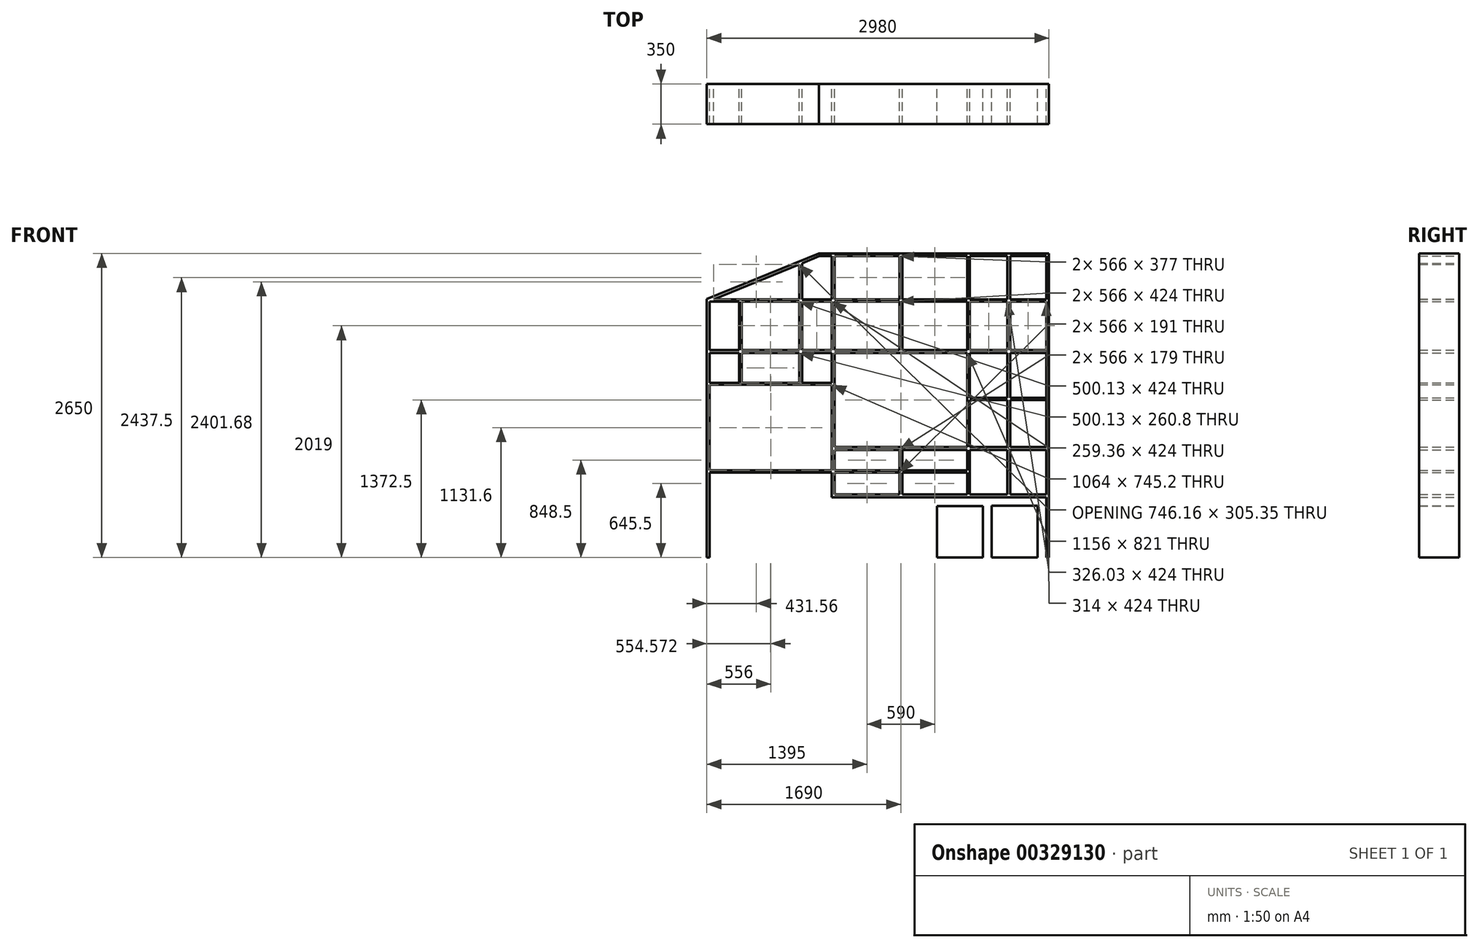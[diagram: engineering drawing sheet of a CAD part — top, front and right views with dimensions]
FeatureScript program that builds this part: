
annotation { "Feature Type Name" : "Feature", "Feature Type Description" : "" }
export const myFeature = defineFeature(function(context is Context, id is Id, definition is map)
    precondition{}
    {
        {
            var Q0;
            Q0=qCreatedBy(makeId("Front.planeOp"),FACE);
            var sketch = newSketch(context, id + "F0", { "sketchPlane" : qUnion([Q0])});
            skLineSegment(sketch, "E0", {"start": v(0, 0) * mm, "end": v(0, 2251) * mm});
            skLineSegment(sketch, "E1", {"start": v(0, 2251) * mm, "end": v(975, 2650) * mm});
            skLineSegment(sketch, "E2", {"start": v(975, 2650) * mm, "end": v(3933.36, 2650) * mm});
            skLineSegment(sketch, "E3", {"start": v(3933.36, 2650) * mm, "end": v(4900, 2240) * mm});
            skLineSegment(sketch, "E4", {"start": v(4900, 2240) * mm, "end": v(4900, 0) * mm});
            skLineSegment(sketch, "E5", {"start": v(4900, 0) * mm, "end": v(0, 0) * mm});
            skLineSegment(sketch, "E6", {"start": v(4550, 0) * mm, "end": v(4550, 2100) * mm});
            skLineSegment(sketch, "E7", {"start": v(4550, 2100) * mm, "end": v(3350, 2100) * mm});
            skLineSegment(sketch, "E8", {"start": v(3350, 2100) * mm, "end": v(3350, 0) * mm});
            skLineSegment(sketch, "E9.bottom", {"start": v(1200, 1695) * mm, "end": v(2180, 1695) * mm});
            skLineSegment(sketch, "E9.top", {"start": v(1200, 1050) * mm, "end": v(2180, 1050) * mm});
            skLineSegment(sketch, "E9.left", {"start": v(1200, 1695) * mm, "end": v(1200, 1050) * mm});
            skLineSegment(sketch, "E9.right", {"start": v(2180, 1695) * mm, "end": v(2180, 1050) * mm});
            skLineSegment(sketch, "E10", {"start": v(2980, 2650) * mm, "end": v(2980, 0) * mm});
            skLineSegment(sketch, "E11", {"start": v(2963, 550) * mm, "end": v(2642, 550) * mm});
            skLineSegment(sketch, "E12.0", {"start": v(24, 0) * mm, "end": v(24, 502) * mm});
            skLineSegment(sketch, "E13.0", {"start": v(979.72, 2626) * mm, "end": v(1088, 2626) * mm});
            skLineSegment(sketch, "E14.0", {"start": v(2963, 526) * mm, "end": v(1088, 526) * mm});
            skLineSegment(sketch, "E15.0", {"start": v(2642, 2636) * mm, "end": v(2642, 2626) * mm});
            skLineSegment(sketch, "E16.0", {"start": v(2291.97, 1807) * mm, "end": v(2291.97, 2231) * mm});
            skLineSegment(sketch, "E17.0", {"start": v(2268, 1807) * mm, "end": v(2268, 2231) * mm});
            skLineSegment(sketch, "E18.0", {"start": v(2268, 1783) * mm, "end": v(2268, 962) * mm});
            skLineSegment(sketch, "E19.0", {"start": v(2292, 1783) * mm, "end": v(2292, 1390.5) * mm});
            skLineSegment(sketch, "E20.0", {"start": v(2292, 938) * mm, "end": v(2292, 540) * mm});
            skLineSegment(sketch, "E21.0", {"start": v(2268, 938) * mm, "end": v(2268, 759) * mm});
            skLineSegment(sketch, "E22.0", {"start": v(1702, 1800) * mm, "end": v(1702, 2231) * mm});
            skLineSegment(sketch, "E23.0", {"start": v(1678, 1800) * mm, "end": v(1678, 2231) * mm});
            skLineSegment(sketch, "E24.0", {"start": v(1112, 1807) * mm, "end": v(1112, 2231) * mm});
            skLineSegment(sketch, "E25.0", {"start": v(1088, 1807) * mm, "end": v(1088, 2231) * mm});
            skLineSegment(sketch, "E26.0", {"start": v(1088, 1783) * mm, "end": v(1088, 1522.2) * mm});
            skLineSegment(sketch, "E27.0", {"start": v(1112, 1783) * mm, "end": v(1112, 1222.6) * mm});
            skLineSegment(sketch, "E28.0", {"start": v(1088, 938) * mm, "end": v(1088, 759) * mm});
            skLineSegment(sketch, "E29.0", {"start": v(1112, 938) * mm, "end": v(1112, 759) * mm});
            skLineSegment(sketch, "E30.0", {"start": v(1105, 1783) * mm, "end": v(2275, 1783) * mm});
            skLineSegment(sketch, "E31.0", {"start": v(1105, 1807) * mm, "end": v(1678, 1807) * mm});
            skLineSegment(sketch, "E32.0", {"start": v(1105, 938) * mm, "end": v(1678, 938) * mm});
            skLineSegment(sketch, "E33.0", {"start": v(1105, 962) * mm, "end": v(2275, 962) * mm});
            skLineSegment(sketch, "E34.0", {"start": v(1095, 1807) * mm, "end": v(822.04, 1807) * mm});
            skLineSegment(sketch, "E35.0", {"start": v(1095, 1783) * mm, "end": v(822.04, 1783) * mm});
            skLineSegment(sketch, "E36.0", {"start": v(2284.97, 938) * mm, "end": v(2625, 938) * mm});
            skLineSegment(sketch, "E37.0", {"start": v(2284.97, 962) * mm, "end": v(2625, 962) * mm});
            skLineSegment(sketch, "E38.0", {"start": v(2284.97, 1783) * mm, "end": v(2625, 1783) * mm});
            skLineSegment(sketch, "E39.0", {"start": v(2284.97, 1807) * mm, "end": v(2625, 1807) * mm});
            skLineSegment(sketch, "E40.0", {"start": v(1678, 945) * mm, "end": v(1678, 759) * mm});
            skLineSegment(sketch, "E41.0", {"start": v(1702, 945) * mm, "end": v(1702, 759) * mm});
            skLineSegment(sketch, "E42.0", {"start": v(17, 2231) * mm, "end": v(280.5, 2231) * mm});
            skLineSegment(sketch, "E43.0", {"start": v(17, 2249) * mm, "end": v(298.67, 2249) * mm});
            skLineSegment(sketch, "E44.0", {"start": v(1095, 1522.2) * mm, "end": v(828.64, 1522.2) * mm});
            skLineSegment(sketch, "E45.0", {"start": v(1095, 1504.2) * mm, "end": v(1088, 1504.2) * mm});
            skLineSegment(sketch, "E46.0", {"start": v(2275, 759) * mm, "end": v(1695, 759) * mm});
            skLineSegment(sketch, "E47.0", {"start": v(2275, 741) * mm, "end": v(1695, 741) * mm});
            skLineSegment(sketch, "E48", {"start": v(1112, 1222.6) * mm, "end": v(1112, 962) * mm});
            skLineSegment(sketch, "E49.bottom", {"start": v(100, 0) * mm, "end": v(500, 0) * mm});
            skLineSegment(sketch, "E49.left", {"start": v(100, 0) * mm, "end": v(100, 450) * mm});
            skLineSegment(sketch, "E49.right", {"start": v(500, 0) * mm, "end": v(500, 450) * mm});
            skLineSegment(sketch, "E50.bottom", {"start": v(576, 0) * mm, "end": v(976, 0) * mm});
            skLineSegment(sketch, "E50.left", {"start": v(576, 0) * mm, "end": v(576, 450) * mm});
            skLineSegment(sketch, "E50.right", {"start": v(976, 0) * mm, "end": v(976, 450) * mm});
            skLineSegment(sketch, "E51.bottom", {"start": v(1052, 0) * mm, "end": v(1452, 0) * mm});
            skLineSegment(sketch, "E51.top", {"start": v(1052, 450) * mm, "end": v(1452, 450) * mm});
            skLineSegment(sketch, "E51.left", {"start": v(1052, 0) * mm, "end": v(1052, 450) * mm});
            skLineSegment(sketch, "E51.right", {"start": v(1452, 0) * mm, "end": v(1452, 450) * mm});
            skLineSegment(sketch, "E52.bottom", {"start": v(1528, 0) * mm, "end": v(1928, 0) * mm});
            skLineSegment(sketch, "E52.top", {"start": v(1528, 450) * mm, "end": v(1928, 450) * mm});
            skLineSegment(sketch, "E52.left", {"start": v(1528, 0) * mm, "end": v(1528, 450) * mm});
            skLineSegment(sketch, "E52.right", {"start": v(1928, 0) * mm, "end": v(1928, 450) * mm});
            skLineSegment(sketch, "E53.bottom", {"start": v(2004, -2.2) * mm, "end": v(2404, -2.2) * mm});
            skLineSegment(sketch, "E53.top", {"start": v(2004, 447.8) * mm, "end": v(2404, 447.8) * mm});
            skLineSegment(sketch, "E53.left", {"start": v(2004, -2.2) * mm, "end": v(2004, 447.8) * mm});
            skLineSegment(sketch, "E53.right", {"start": v(2404, -2.2) * mm, "end": v(2404, 447.8) * mm});
            skLineSegment(sketch, "E54.bottom", {"start": v(2450, 0) * mm, "end": v(2850, 0) * mm});
            skLineSegment(sketch, "E55.bottom", {"start": v(2480, 0) * mm, "end": v(2880, 0) * mm});
            skLineSegment(sketch, "E55.top", {"start": v(2480, 450) * mm, "end": v(2880, 450) * mm});
            skLineSegment(sketch, "E55.left", {"start": v(2480, 0) * mm, "end": v(2480, 450) * mm});
            skLineSegment(sketch, "E55.right", {"start": v(2880, 0) * mm, "end": v(2880, 450) * mm});
            skLineSegment(sketch, "E56", {"start": v(2642, 2636) * mm, "end": v(2618, 2636) * mm});
            skLineSegment(sketch, "E57.trimOffspring", {"start": v(2642, 2626) * mm, "end": v(2956, 2626) * mm});
            skLineSegment(sketch, "E58", {"start": v(2956, 2626) * mm, "end": v(2980, 2650) * mm});
            skLineSegment(sketch, "E59", {"start": v(2963, 2249) * mm, "end": v(2963, 2231) * mm});
            skLineSegment(sketch, "E60.trimOffspring", {"start": v(2956, 2231) * mm, "end": v(2956, 1807) * mm});
            skLineSegment(sketch, "E61", {"start": v(2635, 2249) * mm, "end": v(2635, 2231) * mm});
            skLineSegment(sketch, "E62", {"start": v(2625, 2249) * mm, "end": v(2625, 2231) * mm});
            skLineSegment(sketch, "E63.trimOffspring", {"start": v(2635, 2249) * mm, "end": v(2963, 2249) * mm});
            skLineSegment(sketch, "E64.trimOffspring", {"start": v(2635, 2231) * mm, "end": v(2963, 2231) * mm});
            skLineSegment(sketch, "E65.trimOffspring", {"start": v(2618, 2231) * mm, "end": v(2618, 1807) * mm});
            skLineSegment(sketch, "E66.trimOffspring", {"start": v(2642, 2231) * mm, "end": v(2642, 1807) * mm});
            skLineSegment(sketch, "E67", {"start": v(1112, 2636) * mm, "end": v(1088, 2636) * mm});
            skLineSegment(sketch, "E68.trimOffspring", {"start": v(1112, 2626) * mm, "end": v(1678, 2626) * mm});
            skLineSegment(sketch, "E69", {"start": v(1702, 2636) * mm, "end": v(1678, 2636) * mm});
            skLineSegment(sketch, "E70.trimOffspring", {"start": v(1702, 2626) * mm, "end": v(2268, 2626) * mm});
            skLineSegment(sketch, "E71", {"start": v(2291.97, 2636) * mm, "end": v(2268, 2636) * mm});
            skLineSegment(sketch, "E72.trimOffspring", {"start": v(2291.97, 2626) * mm, "end": v(2618, 2626) * mm});
            skLineSegment(sketch, "E73.trimOffspring", {"start": v(17, 2249) * mm, "end": v(17, 2231) * mm});
            skLineSegment(sketch, "E74", {"start": v(17, 1807) * mm, "end": v(17, 1783) * mm});
            skLineSegment(sketch, "E75.trimOffspring", {"start": v(17, 759) * mm, "end": v(17, 741) * mm});
            skLineSegment(sketch, "E76.trimOffspring", {"start": v(24, 759) * mm, "end": v(24, 1504.2) * mm});
            skLineSegment(sketch, "E77.trimOffspring", {"start": v(17, 1522.2) * mm, "end": v(17, 1504.2) * mm});
            skLineSegment(sketch, "E78.trimOffspring", {"start": v(24, 1522.2) * mm, "end": v(24, 1783) * mm});
            skLineSegment(sketch, "E79.trimOffspring", {"start": v(24, 1807) * mm, "end": v(24, 2231) * mm});
            skLineSegment(sketch, "E80.trimOffspring", {"start": v(24, 502) * mm, "end": v(24, 741) * mm});
            skLineSegment(sketch, "E81", {"start": v(2642, 540) * mm, "end": v(2618, 540) * mm});
            skLineSegment(sketch, "E82.trimOffspring", {"start": v(2618, 550) * mm, "end": v(2292, 550) * mm});
            skLineSegment(sketch, "E83.trimOffspring", {"start": v(2292, 540) * mm, "end": v(2268, 540) * mm});
            skLineSegment(sketch, "E84.trimOffspring", {"start": v(2268, 550) * mm, "end": v(1702, 550) * mm});
            skLineSegment(sketch, "E85.trimOffspring", {"start": v(1702, 540) * mm, "end": v(1678, 540) * mm});
            skLineSegment(sketch, "E86.trimOffspring", {"start": v(1678, 550) * mm, "end": v(1112, 550) * mm});
            skLineSegment(sketch, "E87", {"start": v(2963, 1807) * mm, "end": v(2963, 1783) * mm});
            skLineSegment(sketch, "E88.trimOffspring", {"start": v(2963, 1390.5) * mm, "end": v(2963, 1372.5) * mm});
            skLineSegment(sketch, "E89.trimOffspring", {"start": v(2956, 938) * mm, "end": v(2956, 550) * mm});
            skLineSegment(sketch, "E90.trimOffspring", {"start": v(2956, 1783) * mm, "end": v(2956, 1390.5) * mm});
            skLineSegment(sketch, "E91.trimOffspring", {"start": v(2818.11, 1783) * mm, "end": v(2963, 1783) * mm});
            skLineSegment(sketch, "E92", {"start": v(2635, 1807) * mm, "end": v(2635, 1783) * mm});
            skLineSegment(sketch, "E93.trimOffspring", {"start": v(2635, 938) * mm, "end": v(2963, 938) * mm});
            skLineSegment(sketch, "E94.trimOffspring", {"start": v(2642, 938) * mm, "end": v(2642, 540) * mm});
            skLineSegment(sketch, "E95.trimOffspring", {"start": v(2635, 962) * mm, "end": v(2818.11, 962) * mm});
            skLineSegment(sketch, "E96.trimOffspring", {"start": v(2635, 1390.5) * mm, "end": v(2635, 1372.5) * mm});
            skLineSegment(sketch, "E97.trimOffspring", {"start": v(2635, 1807) * mm, "end": v(2963, 1807) * mm});
            skLineSegment(sketch, "E98.trimOffspring", {"start": v(2635, 1783) * mm, "end": v(2818.11, 1783) * mm});
            skLineSegment(sketch, "E99.trimOffspring", {"start": v(2642, 1783) * mm, "end": v(2642, 1390.5) * mm});
            skLineSegment(sketch, "E100", {"start": v(2625, 1807) * mm, "end": v(2625, 1783) * mm});
            skLineSegment(sketch, "E101.trimOffspring", {"start": v(2625, 1390.5) * mm, "end": v(2625, 1372.5) * mm});
            skLineSegment(sketch, "E102.trimOffspring", {"start": v(2618, 1783) * mm, "end": v(2618, 1390.5) * mm});
            skLineSegment(sketch, "E103.trimOffspring", {"start": v(2618, 938) * mm, "end": v(2618, 540) * mm});
            skLineSegment(sketch, "E104.trimOffspring", {"start": v(2818.11, 962) * mm, "end": v(2963, 962) * mm});
            skLineSegment(sketch, "E105", {"start": v(1702, 1800) * mm, "end": v(1678, 1800) * mm});
            skLineSegment(sketch, "E106.trimOffspring", {"start": v(1702, 1807) * mm, "end": v(2275, 1807) * mm});
            skLineSegment(sketch, "E107", {"start": v(2275, 741) * mm, "end": v(2275, 759) * mm});
            skLineSegment(sketch, "E108.trimOffspring", {"start": v(2284.97, 2249) * mm, "end": v(2284.97, 2231) * mm});
            skLineSegment(sketch, "E109.trimOffspring", {"start": v(2284.97, 2249) * mm, "end": v(2625, 2249) * mm});
            skLineSegment(sketch, "E110.trimOffspring", {"start": v(2284.97, 2231) * mm, "end": v(2625, 2231) * mm});
            skLineSegment(sketch, "E111.trimOffspring", {"start": v(2284.97, 1807) * mm, "end": v(2284.97, 1783) * mm});
            skLineSegment(sketch, "E112.trimOffspring", {"start": v(2275, 2231) * mm, "end": v(2275, 2249) * mm});
            skLineSegment(sketch, "E113.trimOffspring", {"start": v(2284.97, 1390.5) * mm, "end": v(2284.97, 1372.5) * mm});
            skLineSegment(sketch, "E114.trimOffspring", {"start": v(2275, 1783) * mm, "end": v(2275, 1807) * mm});
            skLineSegment(sketch, "E115.trimOffspring", {"start": v(2275, 938) * mm, "end": v(2275, 962) * mm});
            skLineSegment(sketch, "E116.trimOffspring", {"start": v(2268, 741) * mm, "end": v(2268, 540) * mm});
            skLineSegment(sketch, "E117.trimOffspring", {"start": v(2956, 502) * mm, "end": v(2956, 0) * mm});
            skLineSegment(sketch, "E118", {"start": v(1695, 759) * mm, "end": v(1695, 741) * mm});
            skLineSegment(sketch, "E119", {"start": v(1685, 759) * mm, "end": v(1685, 741) * mm});
            skPoint(sketch, "E119.startSnap0", {"position": v(1685, 759) * mm});
            skLineSegment(sketch, "E120.trimOffspring", {"start": v(1702, 741) * mm, "end": v(1702, 540) * mm});
            skLineSegment(sketch, "E121.trimOffspring", {"start": v(1678, 741) * mm, "end": v(1678, 540) * mm});
            skPoint(sketch, "E122.orphan", {"position": v(1685, 786.7) * mm});
            skLineSegment(sketch, "E123.trimOffspring", {"start": v(1685, 759) * mm, "end": v(1105, 759) * mm});
            skLineSegment(sketch, "E124.trimOffspring", {"start": v(1685, 741) * mm, "end": v(1105, 741) * mm});
            skLineSegment(sketch, "E125", {"start": v(1702, 945) * mm, "end": v(1678, 945) * mm});
            skLineSegment(sketch, "E126.trimOffspring", {"start": v(1702, 938) * mm, "end": v(2275, 938) * mm});
            skLineSegment(sketch, "E127", {"start": v(1695, 2249) * mm, "end": v(1695, 2231) * mm});
            skLineSegment(sketch, "E128", {"start": v(1685, 2249) * mm, "end": v(1685, 2231) * mm});
            skLineSegment(sketch, "E129.trimOffspring", {"start": v(1695, 2249) * mm, "end": v(2275, 2249) * mm});
            skLineSegment(sketch, "E130.trimOffspring", {"start": v(1695, 2231) * mm, "end": v(2275, 2231) * mm});
            skLineSegment(sketch, "E131.trimOffspring", {"start": v(298.67, 2249) * mm, "end": v(811.64, 2249) * mm});
            skLineSegment(sketch, "E132.trimOffspring", {"start": v(304.5, 2231) * mm, "end": v(811.64, 2231) * mm});
            skLineSegment(sketch, "E133.trimOffspring", {"start": v(287.3, 1807) * mm, "end": v(287.3, 1783) * mm});
            skLineSegment(sketch, "E134.trimOffspring", {"start": v(287.3, 1807) * mm, "end": v(17, 1807) * mm});
            skLineSegment(sketch, "E135.trimOffspring", {"start": v(280.5, 1807) * mm, "end": v(280.5, 2236) * mm});
            skLineSegment(sketch, "E136.trimOffspring", {"start": v(304.5, 1807) * mm, "end": v(304.5, 2236) * mm});
            skLineSegment(sketch, "E137.trimOffspring", {"start": v(287.3, 1783) * mm, "end": v(17, 1783) * mm});
            skLineSegment(sketch, "E138.trimOffspring", {"start": v(298.67, 1783) * mm, "end": v(298.67, 1807) * mm});
            skLineSegment(sketch, "E139.trimOffspring", {"start": v(280.5, 1522.2) * mm, "end": v(17, 1522.2) * mm});
            skLineSegment(sketch, "E140.trimOffspring", {"start": v(24, 1504.2) * mm, "end": v(17, 1504.2) * mm});
            skLineSegment(sketch, "E141.trimOffspring", {"start": v(304.5, 1515.2) * mm, "end": v(304.5, 1783) * mm});
            skLineSegment(sketch, "E142.trimOffspring", {"start": v(828.64, 2574.98) * mm, "end": v(828.64, 2249) * mm});
            skLineSegment(sketch, "E143.trimOffspring", {"start": v(804.64, 2565.16) * mm, "end": v(804.64, 2249) * mm});
            skLineSegment(sketch, "E144.trimOffspring", {"start": v(822.04, 2249) * mm, "end": v(1095, 2249) * mm});
            skLineSegment(sketch, "E145.trimOffspring", {"start": v(822.04, 2231) * mm, "end": v(1095, 2231) * mm});
            skLineSegment(sketch, "E146.trimOffspring", {"start": v(811.64, 2249) * mm, "end": v(811.64, 2231) * mm});
            skLineSegment(sketch, "E147.trimOffspring", {"start": v(822.04, 2231) * mm, "end": v(822.04, 2249) * mm});
            skLineSegment(sketch, "E148.trimOffspring", {"start": v(811.64, 1807) * mm, "end": v(811.64, 1783) * mm});
            skLineSegment(sketch, "E149.trimOffspring", {"start": v(804.64, 1783) * mm, "end": v(804.64, 1515.2) * mm});
            skLineSegment(sketch, "E150.trimOffspring", {"start": v(828.64, 1783) * mm, "end": v(828.64, 1515.2) * mm});
            skLineSegment(sketch, "E151.trimOffspring", {"start": v(811.64, 1783) * mm, "end": v(298.67, 1783) * mm});
            skLineSegment(sketch, "E152.trimOffspring", {"start": v(811.64, 1807) * mm, "end": v(298.67, 1807) * mm});
            skLineSegment(sketch, "E153.trimOffspring", {"start": v(822.04, 1783) * mm, "end": v(822.04, 1807) * mm});
            skLineSegment(sketch, "E154", {"start": v(1105, 1807) * mm, "end": v(1105, 1783) * mm});
            skLineSegment(sketch, "E155.trimOffspring", {"start": v(1095, 1807) * mm, "end": v(1095, 1783) * mm});
            skLineSegment(sketch, "E156.trimOffspring", {"start": v(1095, 1522.2) * mm, "end": v(1095, 1504.2) * mm});
            skLineSegment(sketch, "E157.trimOffspring", {"start": v(1088, 1504.2) * mm, "end": v(1088, 1222.6) * mm});
            skLineSegment(sketch, "E158.trimOffspring", {"start": v(1088, 1222.6) * mm, "end": v(1088, 938) * mm});
            skLineSegment(sketch, "E159", {"start": v(1105, 962) * mm, "end": v(1105, 938) * mm});
            skLineSegment(sketch, "E160", {"start": v(1105, 759) * mm, "end": v(1105, 741) * mm});
            skLineSegment(sketch, "E161.trimOffspring", {"start": v(1112, 741) * mm, "end": v(1112, 550) * mm});
            skLineSegment(sketch, "E162", {"start": v(1105, 2249) * mm, "end": v(1105, 2231) * mm});
            skLineSegment(sketch, "E163.trimOffspring", {"start": v(1105, 2249) * mm, "end": v(1685, 2249) * mm});
            skLineSegment(sketch, "E164.trimOffspring", {"start": v(1105, 2231) * mm, "end": v(1685, 2231) * mm});
            skLineSegment(sketch, "E165.trimOffspring", {"start": v(1095, 2249) * mm, "end": v(1095, 2231) * mm});
            skLineSegment(sketch, "E166.trimOffspring", {"start": v(280.5, 1515.2) * mm, "end": v(280.5, 1783) * mm});
            skLineSegment(sketch, "E167", {"start": v(1112, 741) * mm, "end": v(1105, 741) * mm});
            skLineSegment(sketch, "E168", {"start": v(304.5, 1522.2) * mm, "end": v(804.64, 1522.2) * mm});
            skLineSegment(sketch, "E169.0", {"start": v(576, 650) * mm, "end": v(976, 650) * mm});
            skLineSegment(sketch, "E170.0", {"start": v(100, 650) * mm, "end": v(500, 650) * mm});
            skLineSegment(sketch, "E171", {"start": v(500, 650) * mm, "end": v(500, 450) * mm});
            skLineSegment(sketch, "E172", {"start": v(100, 650) * mm, "end": v(100, 450) * mm});
            skLineSegment(sketch, "E173", {"start": v(576, 650) * mm, "end": v(576, 450) * mm});
            skLineSegment(sketch, "E174", {"start": v(976, 650) * mm, "end": v(976, 450) * mm});
            skLineSegment(sketch, "E175", {"start": v(2284.97, 1372.5) * mm, "end": v(2625, 1372.5) * mm});
            skLineSegment(sketch, "E176.0", {"start": v(2284.97, 1390.5) * mm, "end": v(2625, 1390.5) * mm});
            skPoint(sketch, "E177.orphan", {"position": v(2292, 1372.5) * mm});
            skLineSegment(sketch, "E178.trimOffspring", {"start": v(2292, 1372.5) * mm, "end": v(2292, 962) * mm});
            skLineSegment(sketch, "E179.trimOffspring", {"start": v(2284.97, 962) * mm, "end": v(2284.97, 938) * mm});
            skPoint(sketch, "E180.orphan", {"position": v(2956, 1372.5) * mm});
            skLineSegment(sketch, "E181.trimOffspring", {"start": v(2956, 1372.5) * mm, "end": v(2956, 962) * mm});
            skLineSegment(sketch, "E182.trimOffspring", {"start": v(2963, 962) * mm, "end": v(2963, 938) * mm});
            skLineSegment(sketch, "E183", {"start": v(2625, 962) * mm, "end": v(2625, 938) * mm});
            skLineSegment(sketch, "E184", {"start": v(2635, 962) * mm, "end": v(2635, 938) * mm});
            skLineSegment(sketch, "E185.trimOffspring", {"start": v(2642, 1372.5) * mm, "end": v(2642, 962) * mm});
            skLineSegment(sketch, "E186.trimOffspring", {"start": v(2618, 1372.5) * mm, "end": v(2618, 962) * mm});
            skLineSegment(sketch, "E187.trimOffspring", {"start": v(2635, 1372.5) * mm, "end": v(2963, 1372.5) * mm});
            skLineSegment(sketch, "E188.trimOffspring", {"start": v(2635, 1390.5) * mm, "end": v(2963, 1390.5) * mm});
            skLineSegment(sketch, "E189.trimOffspring", {"start": v(804.64, 2231) * mm, "end": v(804.64, 1807) * mm});
            skLineSegment(sketch, "E190.trimOffspring", {"start": v(828.64, 2231) * mm, "end": v(828.64, 1807) * mm});
            skLineSegment(sketch, "E191.trimOffspring", {"start": v(828.64, 2564.17) * mm, "end": v(979.72, 2626) * mm});
            skLineSegment(sketch, "E192.trimOffspring", {"start": v(804.64, 2565.16) * mm, "end": v(828.64, 2574.98) * mm});
            skLineSegment(sketch, "E193", {"start": v(1088, 2636) * mm, "end": v(1088, 2249) * mm});
            skLineSegment(sketch, "E194", {"start": v(1112, 2636) * mm, "end": v(1112, 2249) * mm});
            skLineSegment(sketch, "E195", {"start": v(1678, 2249) * mm, "end": v(1678, 2636) * mm});
            skLineSegment(sketch, "E196", {"start": v(1702, 2636) * mm, "end": v(1702, 2249) * mm});
            skLineSegment(sketch, "E197", {"start": v(2268, 2636) * mm, "end": v(2268, 2249) * mm});
            skLineSegment(sketch, "E198", {"start": v(2291.97, 2249) * mm, "end": v(2291.97, 2636) * mm});
            skLineSegment(sketch, "E199", {"start": v(2618, 2636) * mm, "end": v(2618, 2249) * mm});
            skLineSegment(sketch, "E200", {"start": v(2642, 2626) * mm, "end": v(2642, 2249) * mm});
            skLineSegment(sketch, "E201", {"start": v(2956, 2626) * mm, "end": v(2956, 2249) * mm});
            skLineSegment(sketch, "E202", {"start": v(1112, 550) * mm, "end": v(1088, 526) * mm});
            skLineSegment(sketch, "E203", {"start": v(1095, 759) * mm, "end": v(1095, 741) * mm});
            skLineSegment(sketch, "E204.trimOffspring", {"start": v(1088, 741) * mm, "end": v(1088, 526) * mm});
            skLineSegment(sketch, "E205.trimOffspring", {"start": v(1095, 741) * mm, "end": v(17, 741) * mm});
            skLineSegment(sketch, "E206.trimOffspring", {"start": v(1095, 759) * mm, "end": v(17, 759) * mm});
            skLineSegment(sketch, "E207.0", {"start": v(280.5, 1515.2) * mm, "end": v(304.5, 1515.2) * mm});
            skLineSegment(sketch, "E208.trimOffspring", {"start": v(804.64, 1515.2) * mm, "end": v(828.64, 1515.2) * mm});
            skLineSegment(sketch, "E209", {"start": v(1088, 1504.2) * mm, "end": v(24, 1504.2) * mm});
            skLineSegment(sketch, "E210.0", {"start": v(2963, 550) * mm, "end": v(2963, 526) * mm});
            skLineSegment(sketch, "E211.trimOffspring", {"start": v(2956, 526) * mm, "end": v(2956, 502) * mm});
            skLineSegment(sketch, "E212.trimOffspring", {"start": v(280.5, 2236) * mm, "end": v(304.5, 2236) * mm});
            skLineSegment(sketch, "E213.trimOffspring", {"start": v(58.48, 2249) * mm, "end": v(804.64, 2554.35) * mm});
            skLineSegment(sketch, "E214", {"start": v(17, 2249) * mm, "end": v(0, 2249) * mm});
            skSolve(sketch);
        }
        {
            var Q0;
            {var subQ12=sQuery(id+"F0.wireOp",EDGE,"cc0fc2fd-8950-4ce1-810f-629987963abd.0");Q0=makeQuery(id+"F0.imprint","IMPRINT",FACE,{"disambiguationData":[TD([[makeQuery(id+"F0.imprint","IMPRINT",EDGE,{"derivedFrom":subQ12}),1.0]])]});}
            var Q1;
            {var subQ7=sQuery(id+"F0.wireOp",EDGE,"E13.0");Q1=makeQuery(id+"F0.imprint","IMPRINT",FACE,{"disambiguationData":[TD([[makeQuery(id+"F0.imprint","IMPRINT",EDGE,{"derivedFrom":subQ7}),1.0]])]});}
            var Q2;
            Q2=makeQuery(id+"F0.imprint","IMPRINT",FACE,{"disambiguationData":[TD([[makeQuery(id+"F0.imprint","IMPRINT",EDGE,{"derivedFrom":sQuery(id+"F0.wireOp",EDGE,"E1")}),-1.0]])]});
            var Q3;
            {var subQ12=sQuery(id+"F0.wireOp",EDGE,"Zqx6Wrpy-ailH-Ofh8-OMIL-Cnyi6wDhXa7h");Q3=makeQuery(id+"F0.imprint","IMPRINT",FACE,{"disambiguationData":[TD([[makeQuery(id+"F0.imprint","IMPRINT",EDGE,{"derivedFrom":subQ12}),-1.0]])]});}
            var Q4;
            {var subQ16=sQuery(id+"F0.wireOp",EDGE,"E11");Q4=makeQuery(id+"F0.imprint","IMPRINT",FACE,{"disambiguationData":[TD([[makeQuery(id+"F0.imprint","IMPRINT",EDGE,{"derivedFrom":subQ16}),1.0]])]});}
            var Q5;
            {var subQ4=sQuery(id+"F0.wireOp",EDGE,"E12.0");Q5=makeQuery(id+"F0.imprint","IMPRINT",FACE,{"disambiguationData":[TD([[makeQuery(id+"F0.imprint","IMPRINT",EDGE,{"derivedFrom":subQ4}),1.0]])]});}
            var Q6;
            {var subQ3=sQuery(id+"F0.wireOp",EDGE,"E117.trimOffspring");Q6=makeQuery(id+"F0.imprint","IMPRINT",FACE,{"disambiguationData":[TD([[makeQuery(id+"F0.imprint","IMPRINT",EDGE,{"derivedFrom":subQ3}),1.0]])]});}
            var Q7;
            Q7=makeQuery(id+"F0.imprint","IMPRINT",FACE,{"disambiguationData":[TD([[makeQuery(id+"F0.imprint","IMPRINT",EDGE,{"derivedFrom":sQuery(id+"F0.wireOp",EDGE,"E14.0")}),1.0]])]});
            var Q8;
            Q8=makeQuery(id+"F0.imprint","IMPRINT",FACE,{"disambiguationData":[TD([[makeQuery(id+"F0.imprint","IMPRINT",EDGE,{"derivedFrom":sQuery(id+"F0.wireOp",EDGE,"E15.0")}),-1.0]])]});
            var Q9;
            {var subQ11=sQuery(id+"F0.wireOp",EDGE,"E16.0");Q9=makeQuery(id+"F0.imprint","IMPRINT",FACE,{"disambiguationData":[TD([[makeQuery(id+"F0.imprint","IMPRINT",EDGE,{"derivedFrom":subQ11}),1.0]])]});}
            var Q10;
            {var subQ4=sQuery(id+"F0.wireOp",EDGE,"E69");Q10=makeQuery(id+"F0.imprint","IMPRINT",FACE,{"disambiguationData":[TD([[makeQuery(id+"F0.imprint","IMPRINT",EDGE,{"derivedFrom":subQ4}),1.0]])]});}
            var Q11;
            {var subQ8=sQuery(id+"F0.wireOp",EDGE,"723af7a5-55d7-4603-a10d-ee5387bef70e.trimOffspring");Q11=makeQuery(id+"F0.imprint","IMPRINT",FACE,{"disambiguationData":[TD([[makeQuery(id+"F0.imprint","IMPRINT",EDGE,{"derivedFrom":subQ8}),-1.0]])]});}
            var Q12;
            {var subQ13=sQuery(id+"F0.wireOp",EDGE,"j7I8hBcO-UPLF-qasG-mkQ5-tIXsxcX5kJvB");Q12=makeQuery(id+"F0.imprint","IMPRINT",FACE,{"disambiguationData":[TD([[makeQuery(id+"F0.imprint","IMPRINT",EDGE,{"derivedFrom":subQ13}),-1.0]])]});}
            var Q13;
            {var subQ9=sQuery(id+"F0.wireOp",EDGE,"E85.trimOffspring");Q13=makeQuery(id+"F0.imprint","IMPRINT",FACE,{"disambiguationData":[TD([[makeQuery(id+"F0.imprint","IMPRINT",EDGE,{"derivedFrom":subQ9}),-1.0]])]});}
            var Q14;
            Q14=makeQuery(id+"F0.imprint","IMPRINT",FACE,{"disambiguationData":[TD([[makeQuery(id+"F0.imprint","IMPRINT",EDGE,{"derivedFrom":sQuery(id+"F0.wireOp",EDGE,"E55.top")}),-1.0]])]});
            var Q15;
            {var subQ5=sQuery(id+"F0.wireOp",EDGE,"E53.top");Q15=makeQuery(id+"F0.imprint","IMPRINT",FACE,{"disambiguationData":[TD([[makeQuery(id+"F0.imprint","IMPRINT",EDGE,{"derivedFrom":subQ5}),-1.0]])]});}
            var Q16;
            Q16=makeQuery(id+"F0.imprint","IMPRINT",FACE,{"disambiguationData":[TD([[makeQuery(id+"F0.imprint","IMPRINT",EDGE,{"derivedFrom":sQuery(id+"F0.wireOp",EDGE,"E52.bottom")}),1.0]])]});
            var Q17;
            Q17=makeQuery(id+"F0.imprint","IMPRINT",FACE,{"disambiguationData":[TD([[makeQuery(id+"F0.imprint","IMPRINT",EDGE,{"derivedFrom":sQuery(id+"F0.wireOp",EDGE,"E51.bottom")}),1.0]])]});
            var Q18;
            Q18=makeQuery(id+"F0.imprint","IMPRINT",FACE,{"disambiguationData":[TD([[makeQuery(id+"F0.imprint","IMPRINT",EDGE,{"derivedFrom":sQuery(id+"F0.wireOp",EDGE,"E50.bottom")}),1.0]])]});
            var Q19;
            Q19=makeQuery(id+"F0.imprint","IMPRINT",FACE,{"disambiguationData":[TD([[makeQuery(id+"F0.imprint","IMPRINT",EDGE,{"derivedFrom":sQuery(id+"F0.wireOp",EDGE,"E49.bottom")}),1.0]])]});
            var Q20;
            {var subQ0=sQuery(id+"F0.wireOp",EDGE,"E105");Q20=makeQuery(id+"F0.imprint","IMPRINT",FACE,{"disambiguationData":[TD([[makeQuery(id+"F0.imprint","IMPRINT",EDGE,{"derivedFrom":subQ0}),1.0]])]});}
            var Q21;
            {var subQ4=sQuery(id+"F0.wireOp",EDGE,"E115.trimOffspring");Q21=makeQuery(id+"F0.imprint","IMPRINT",FACE,{"disambiguationData":[TD([[makeQuery(id+"F0.imprint","IMPRINT",EDGE,{"derivedFrom":subQ4}),1.0]])]});}
            var Q22;
            {var subQ9=sQuery(id+"F0.wireOp",EDGE,"E88.trimOffspring");Q22=makeQuery(id+"F0.imprint","IMPRINT",FACE,{"disambiguationData":[TD([[makeQuery(id+"F0.imprint","IMPRINT",EDGE,{"derivedFrom":subQ9}),-1.0]])]});}
            var Q23;
            {var subQ4=sQuery(id+"F0.wireOp",EDGE,"E119");Q23=makeQuery(id+"F0.imprint","IMPRINT",FACE,{"disambiguationData":[TD([[makeQuery(id+"F0.imprint","IMPRINT",EDGE,{"derivedFrom":subQ4}),-1.0]])]});}
            var Q24;
            {var subQ0=sQuery(id+"F0.wireOp",EDGE,"E107");Q24=makeQuery(id+"F0.imprint","IMPRINT",FACE,{"disambiguationData":[TD([[makeQuery(id+"F0.imprint","IMPRINT",EDGE,{"derivedFrom":subQ0}),1.0]])]});}
            var Q25;
            {var subQ4=sQuery(id+"F0.wireOp",EDGE,"E58");Q25=makeQuery(id+"F0.imprint","IMPRINT",FACE,{"disambiguationData":[TD([[makeQuery(id+"F0.imprint","IMPRINT",EDGE,{"derivedFrom":subQ4}),-1.0]])]});}
            var Q26;
            {var subQ11=sQuery(id+"F0.wireOp",EDGE,"E24.0");Q26=makeQuery(id+"F0.imprint","IMPRINT",FACE,{"disambiguationData":[TD([[makeQuery(id+"F0.imprint","IMPRINT",EDGE,{"derivedFrom":subQ11}),1.0]])]});}
            var Q27;
            {var subQ11=sQuery(id+"F0.wireOp",EDGE,"E146.trimOffspring");Q27=makeQuery(id+"F0.imprint","IMPRINT",FACE,{"disambiguationData":[TD([[makeQuery(id+"F0.imprint","IMPRINT",EDGE,{"derivedFrom":subQ11}),1.0]])]});}
            var Q28;
            Q28=makeQuery(id+"F0.imprint","IMPRINT",FACE,{"disambiguationData":[TD([[makeQuery(id+"F0.imprint","IMPRINT",EDGE,{"derivedFrom":sQuery(id+"F0.wireOp",EDGE,"E45.0")}),-1.0]])]});
            var Q29;
            {var subQ6=sQuery(id+"F0.wireOp",EDGE,"4uqoLxak-8dQo-QfdN-CZMn-XK6vGcTCFNYD");Q29=makeQuery(id+"F0.imprint","IMPRINT",FACE,{"disambiguationData":[TD([[makeQuery(id+"F0.imprint","IMPRINT",EDGE,{"derivedFrom":subQ6}),1.0]])]});}
            var Q30;
            {var subQ1=sQuery(id+"F0.wireOp",EDGE,"E133.trimOffspring");Q30=makeQuery(id+"F0.imprint","IMPRINT",FACE,{"disambiguationData":[TD([[makeQuery(id+"F0.imprint","IMPRINT",EDGE,{"derivedFrom":subQ1}),1.0]])]});}
            var Q31;
            {var subQ11=sQuery(id+"F0.wireOp",EDGE,"E73.trimOffspring");Q31=makeQuery(id+"F0.imprint","IMPRINT",FACE,{"disambiguationData":[TD([[makeQuery(id+"F0.imprint","IMPRINT",EDGE,{"derivedFrom":subQ11}),-1.0]])]});}
            var Q32;
            {var subQ4=sQuery(id+"F0.wireOp",EDGE,"E75.trimOffspring");Q32=makeQuery(id+"F0.imprint","IMPRINT",FACE,{"disambiguationData":[TD([[makeQuery(id+"F0.imprint","IMPRINT",EDGE,{"derivedFrom":subQ4}),1.0]])]});}
            var Q33;
            {var subQ4=sQuery(id+"F0.wireOp",EDGE,"E138.trimOffspring");Q33=makeQuery(id+"F0.imprint","IMPRINT",FACE,{"disambiguationData":[TD([[makeQuery(id+"F0.imprint","IMPRINT",EDGE,{"derivedFrom":subQ4}),-1.0]])]});}
            var Q34;
            {var subQ3=sQuery(id+"F0.wireOp",EDGE,"E153.trimOffspring");Q34=makeQuery(id+"F0.imprint","IMPRINT",FACE,{"disambiguationData":[TD([[makeQuery(id+"F0.imprint","IMPRINT",EDGE,{"derivedFrom":subQ3}),-1.0]])]});}
            var Q35;
            {var subQ4=sQuery(id+"F0.wireOp",EDGE,"E74");Q35=makeQuery(id+"F0.imprint","IMPRINT",FACE,{"disambiguationData":[TD([[makeQuery(id+"F0.imprint","IMPRINT",EDGE,{"derivedFrom":subQ4}),1.0]])]});}
            var Q36;
            {var subQ0=sQuery(id+"F0.wireOp",EDGE,"E179.trimOffspring");Q36=makeQuery(id+"F0.imprint","IMPRINT",FACE,{"disambiguationData":[TD([[makeQuery(id+"F0.imprint","IMPRINT",EDGE,{"derivedFrom":subQ0}),1.0]])]});}
            var Q37;
            {var subQ4=sQuery(id+"F0.wireOp",EDGE,"E101.trimOffspring");Q37=makeQuery(id+"F0.imprint","IMPRINT",FACE,{"disambiguationData":[TD([[makeQuery(id+"F0.imprint","IMPRINT",EDGE,{"derivedFrom":subQ4}),-1.0]])]});}
            var Q38;
            {var subQ3=sQuery(id+"F0.wireOp",EDGE,"E100");Q38=makeQuery(id+"F0.imprint","IMPRINT",FACE,{"disambiguationData":[TD([[makeQuery(id+"F0.imprint","IMPRINT",EDGE,{"derivedFrom":subQ3}),-1.0]])]});}
            var Q39;
            {var subQ4=sQuery(id+"F0.wireOp",EDGE,"E62");Q39=makeQuery(id+"F0.imprint","IMPRINT",FACE,{"disambiguationData":[TD([[makeQuery(id+"F0.imprint","IMPRINT",EDGE,{"derivedFrom":subQ4}),-1.0]])]});}
            var Q40;
            {var subQ4=sQuery(id+"F0.wireOp",EDGE,"E59");Q40=makeQuery(id+"F0.imprint","IMPRINT",FACE,{"disambiguationData":[TD([[makeQuery(id+"F0.imprint","IMPRINT",EDGE,{"derivedFrom":subQ4}),-1.0]])]});}
            var Q41;
            {var subQ4=sQuery(id+"F0.wireOp",EDGE,"E112.trimOffspring");Q41=makeQuery(id+"F0.imprint","IMPRINT",FACE,{"disambiguationData":[TD([[makeQuery(id+"F0.imprint","IMPRINT",EDGE,{"derivedFrom":subQ4}),1.0]])]});}
            var Q42;
            {var subQ4=sQuery(id+"F0.wireOp",EDGE,"E128");Q42=makeQuery(id+"F0.imprint","IMPRINT",FACE,{"disambiguationData":[TD([[makeQuery(id+"F0.imprint","IMPRINT",EDGE,{"derivedFrom":subQ4}),-1.0]])]});}
            var Q43;
            {var subQ0=sQuery(id+"F0.wireOp",EDGE,"E147.trimOffspring");Q43=makeQuery(id+"F0.imprint","IMPRINT",FACE,{"disambiguationData":[TD([[makeQuery(id+"F0.imprint","IMPRINT",EDGE,{"derivedFrom":subQ0}),-1.0]])]});}
            var Q44;
            {var subQ10=sQuery(id+"F0.wireOp",EDGE,"E73.trimOffspring");Q44=makeQuery(id+"F0.imprint","IMPRINT",FACE,{"disambiguationData":[TD([[makeQuery(id+"F0.imprint","IMPRINT",EDGE,{"derivedFrom":subQ10}),1.0]])]});}
            var Q45;
            {var subQ3=sQuery(id+"F0.wireOp",EDGE,"E87");Q45=makeQuery(id+"F0.imprint","IMPRINT",FACE,{"disambiguationData":[TD([[makeQuery(id+"F0.imprint","IMPRINT",EDGE,{"derivedFrom":subQ3}),-1.0]])]});}
            var Q46;
            {var subQ2=sQuery(id+"F0.wireOp",EDGE,"E182.trimOffspring");Q46=makeQuery(id+"F0.imprint","IMPRINT",FACE,{"disambiguationData":[TD([[makeQuery(id+"F0.imprint","IMPRINT",EDGE,{"derivedFrom":subQ2}),-1.0]])]});}
            extrude(context, id + "F1", {"entities" : qUnion([Q0, Q1, Q2, Q3, Q4, Q5, Q6, Q7, Q8, Q9, Q10, Q11, Q12, Q13, Q14, Q15, Q16, Q17, Q18, Q19, Q20, Q21, Q22, Q23, Q24, Q25, Q26, Q27, Q28, Q29, Q30, Q31, Q32, Q33, Q34, Q35, Q36, Q37, Q38, Q39, Q40, Q41, Q42, Q43, Q44, Q45, Q46]), "depth" : 350 * mm, "offsetDistance" : 25 * mm});
        }
    });
